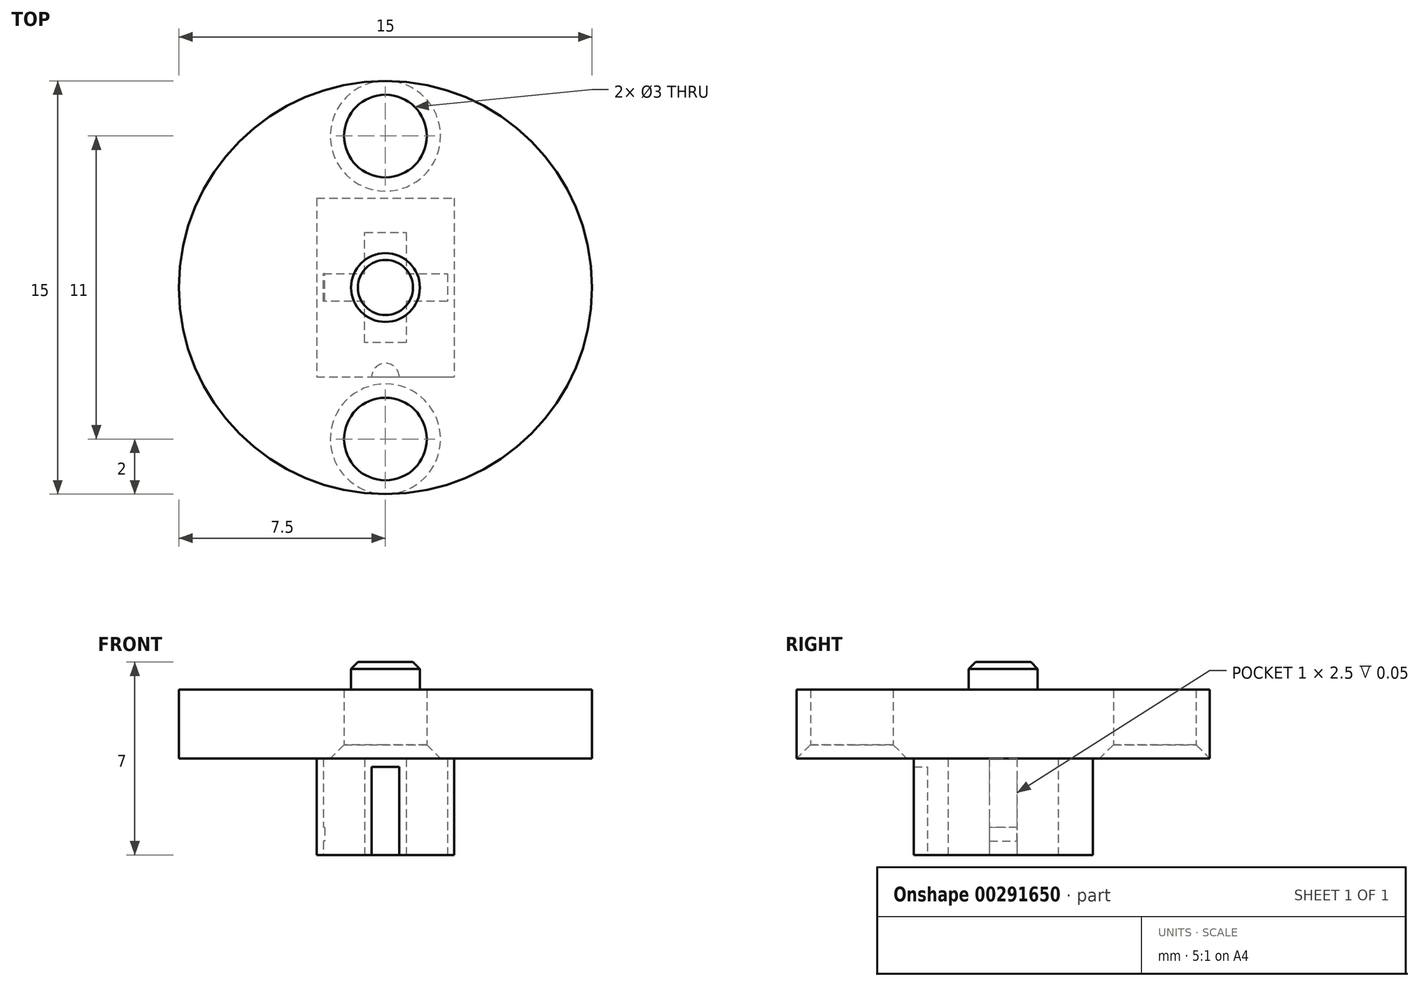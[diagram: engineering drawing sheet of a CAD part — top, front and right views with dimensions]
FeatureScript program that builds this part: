
annotation { "Feature Type Name" : "Feature", "Feature Type Description" : "" }
export const myFeature = defineFeature(function(context is Context, id is Id, definition is map)
    precondition{}
    {
        {
            var Q0;
            Q0=qCreatedBy(makeId("Top.planeOp"),FACE);
            var sketch = newSketch(context, id + "F0", { "sketchPlane" : qUnion([Q0])});
            skLineSegment(sketch, "E0", {"start": v(-0.75, -0.5) * mm, "end": v(-2.25, -0.5) * mm});
            skLineSegment(sketch, "E1", {"start": v(-2.25, -0.5) * mm, "end": v(-2.25, 0.5) * mm});
            skLineSegment(sketch, "E2", {"start": v(-2.25, 0.5) * mm, "end": v(-0.75, 0.5) * mm});
            skLineSegment(sketch, "E3", {"start": v(-0.75, 0.5) * mm, "end": v(-0.75, 2) * mm});
            skLineSegment(sketch, "E4", {"start": v(-0.75, 2) * mm, "end": v(0.75, 2) * mm});
            skLineSegment(sketch, "E5", {"start": v(0.75, 2) * mm, "end": v(0.75, 0.5) * mm});
            skLineSegment(sketch, "E6", {"start": v(0.75, 0.5) * mm, "end": v(2.25, 0.5) * mm});
            skLineSegment(sketch, "E7", {"start": v(2.25, 0.5) * mm, "end": v(2.25, -0.5) * mm});
            skLineSegment(sketch, "E8", {"start": v(2.25, -0.5) * mm, "end": v(0.75, -0.5) * mm});
            skLineSegment(sketch, "E9", {"start": v(0.75, -0.5) * mm, "end": v(0.75, -2) * mm});
            skLineSegment(sketch, "E10", {"start": v(0.75, -2) * mm, "end": v(-0.75, -2) * mm});
            skLineSegment(sketch, "E11", {"start": v(-0.75, -2) * mm, "end": v(-0.75, -0.5) * mm});
            skLineSegment(sketch, "E12.bottom", {"start": v(-2.5, 3.25) * mm, "end": v(2.5, 3.25) * mm});
            skLineSegment(sketch, "E12.top", {"start": v(-2.5, -3.25) * mm, "end": v(2.5, -3.25) * mm});
            skLineSegment(sketch, "E12.left", {"start": v(-2.5, 3.25) * mm, "end": v(-2.5, -3.25) * mm});
            skLineSegment(sketch, "E12.right", {"start": v(2.5, 3.25) * mm, "end": v(2.5, -3.25) * mm});
            skSolve(sketch);
        }
        {
            var Q0;
            Q0=makeQuery(id+"F0.imprint","IMPRINT",FACE,{"disambiguationData":[TD([[makeQuery(id+"F0.imprint","IMPRINT",EDGE,{"derivedFrom":sQuery(id+"F0.wireOp",EDGE,"E0")}),1.0]])]});
            extrude(context, id + "F1", {"entities" : qUnion([Q0]), "depth" : 3.5 * mm});
        }
        {
            var Q0;
            Q0=makeQuery(id+"F1.opExtrude","CAP_FACE",FACE,{"disambiguationData":[OSD([sQuery(id+"F0.wireOp",EDGE,"E0"),sQuery(id+"F0.wireOp",EDGE,"E1"),sQuery(id+"F0.wireOp",EDGE,"E2"),sQuery(id+"F0.wireOp",EDGE,"E3"),sQuery(id+"F0.wireOp",EDGE,"E4"),sQuery(id+"F0.wireOp",EDGE,"E5"),sQuery(id+"F0.wireOp",EDGE,"E6"),sQuery(id+"F0.wireOp",EDGE,"E7"),sQuery(id+"F0.wireOp",EDGE,"E8"),sQuery(id+"F0.wireOp",EDGE,"E9"),sQuery(id+"F0.wireOp",EDGE,"E10"),sQuery(id+"F0.wireOp",EDGE,"E11"),sQuery(id+"F0.wireOp",EDGE,"xdch3Cf1-flaN-mxDd-AqKS-SK6m0hY20tAS")])],"isStart":false});
            var sketch = newSketch(context, id + "F2", { "sketchPlane" : qUnion([Q0])});
            skCircle(sketch, "E13", {"center": v(0, 0) * mm, "radius": 7.5 * mm});
            skCircle(sketch, "E14", {"center": v(0, 5.5) * mm, "radius": 1.5 * mm});
            skCircle(sketch, "E15", {"center": v(0, -5.5) * mm, "radius": 1.5 * mm});
            skSolve(sketch);
        }
        {
            var Q0;
            Q0=makeQuery(id+"F2.imprint","IMPRINT",FACE,{"disambiguationData":[TD([[makeQuery(id+"F2.imprint","IMPRINT",EDGE,{"derivedFrom":makeQuery(id+"F1.opExtrude","CAP_EDGE",EDGE,{"disambiguationData":[OSD([sQuery(id+"F0.wireOp",EDGE,"E0")])],"isStart":false})}),-1.0]])]});
            var Q1;
            Q1=makeQuery(id+"F2.imprint","IMPRINT",FACE,{"disambiguationData":[TD([[makeQuery(id+"F2.imprint","IMPRINT",EDGE,{"derivedFrom":makeQuery(id+"F1.opExtrude","CAP_EDGE",EDGE,{"disambiguationData":[OSD([sQuery(id+"F0.wireOp",EDGE,"E0")])],"isStart":false})}),1.0]])]});
            var Q2;
            Q2=makeQuery(id+"F2.imprint","IMPRINT",FACE,{"disambiguationData":[TD([[makeQuery(id+"F2.imprint","IMPRINT",EDGE,{"derivedFrom":sQuery(id+"F2.wireOp",EDGE,"E13")}),1.0]])]});
            var Q3;
            Q3=sQuery(id+"F2.wireOp",EDGE,"E13");
            var Q4;
            Q4=sQuery(id+"F2.wireOp",EDGE,"E14");
            var Q5;
            Q5=sQuery(id+"F2.wireOp",EDGE,"E15");
            extrude(context, id + "F3", {"entities" : qUnion([Q0, Q1, Q2]), "operationType" : NewBodyOperationType.ADD, "surfaceEntities" : qUnion([Q3, Q4, Q5]), "depth" : 2.5 * mm});
        }
        {
            var Q0;
            Q0=makeQuery(id+"F3.opExtrude","CAP_FACE",FACE,{"disambiguationData":[OSD([sQuery(id+"F2.wireOp",EDGE,"E13"),sQuery(id+"F2.wireOp",EDGE,"E14"),sQuery(id+"F2.wireOp",EDGE,"E15")])],"isStart":false});
            var sketch = newSketch(context, id + "F4", { "sketchPlane" : qUnion([Q0])});
            skCircle(sketch, "E16", {"center": v(0, 0) * mm, "radius": 1.25 * mm});
            skSolve(sketch);
        }
        {
            var Q0;
            Q0=makeQuery(id+"F4.imprint","IMPRINT",FACE,{"disambiguationData":[TD([[makeQuery(id+"F4.imprint","IMPRINT",EDGE,{"derivedFrom":sQuery(id+"F4.wireOp",EDGE,"E16")}),1.0]])]});
            extrude(context, id + "F5", {"entities" : qUnion([Q0]), "operationType" : NewBodyOperationType.ADD, "depth" : 1 * mm});
        }
        {
            var Q0;
            Q0=makeQuery(id+"F3.opExtrude","CAP_EDGE",EDGE,{"disambiguationData":[OSD([sQuery(id+"F2.wireOp",EDGE,"E14")])],"isStart":true});
            var Q1;
            Q1=makeQuery(id+"F3.opExtrude","CAP_EDGE",EDGE,{"disambiguationData":[OSD([sQuery(id+"F2.wireOp",EDGE,"E15")])],"isStart":true});
            chamfer(context, id + "F6", {"entities" : qUnion([Q0, Q1]), "width" : 0.5 * mm, "tangentPropagation" : true});
        }
        {
            var Q0;
            Q0=makeQuery(id+"F5.opExtrude","CAP_EDGE",EDGE,{"disambiguationData":[OSD([sQuery(id+"F4.wireOp",EDGE,"E16")])],"isStart":false});
            chamfer(context, id + "F7", {"entities" : qUnion([Q0]), "width" : 0.25 * mm, "tangentPropagation" : true});
        }
        {
            var Q0;
            Q0=makeQuery(id+"F1.opExtrude","SWEPT_FACE",FACE,{"disambiguationData":[OSD([sQuery(id+"F0.wireOp",EDGE,"E12.left")])]});
            var sketch = newSketch(context, id + "F8", { "sketchPlane" : qUnion([Q0])});
            skLineSegment(sketch, "E17", {"start": v(0.5, 0) * mm, "end": v(0.5, 0.5) * mm});
            skLineSegment(sketch, "E18", {"start": v(0.5, 0.5) * mm, "end": v(-0.5, 0.5) * mm});
            skLineSegment(sketch, "E19", {"start": v(-0.5, 0.5) * mm, "end": v(-0.5, 1) * mm});
            skLineSegment(sketch, "E20", {"start": v(-0.5, 1) * mm, "end": v(0.5, 1) * mm});
            skLineSegment(sketch, "E21", {"start": v(0.5, 1) * mm, "end": v(0.5, 0.5) * mm});
            skSolve(sketch);
        }
        {
            var Q0;
            Q0 = qSketchRegion(id + "F8", true);
            var Q1;
            Q1=makeQuery(id+"F8.imprint","IMPRINT",FACE,{"disambiguationData":[TD([[makeQuery(id+"F8.imprint","IMPRINT",EDGE,{"derivedFrom":sQuery(id+"F8.wireOp",EDGE,"E18")}),-1.0]])]});
            extrude(context, id + "F9", {"entities" : qUnion([Q0, Q1]), "operationType" : NewBodyOperationType.ADD, "oppositeDirection" : true, "depth" : 0.3 * mm});
        }
        {
            var Q0;
            Q0=makeQuery(id+"F0.imprint","IMPRINT",FACE,{"disambiguationData":[TD([[makeQuery(id+"F0.imprint","IMPRINT",EDGE,{"derivedFrom":sQuery(id+"F0.wireOp",EDGE,"E0")}),1.0]])]});
            var sketch = newSketch(context, id + "F10", { "sketchPlane" : qUnion([Q0])});
            skCircle(sketch, "E22", {"center": v(0, -3.25) * mm, "radius": 0.5 * mm});
            skSolve(sketch);
        }
        {
            var Q0;
            Q0 = qSketchRegion(id + "F10", true);
            extrude(context, id + "F11", {"entities" : qUnion([Q0]), "operationType" : NewBodyOperationType.REMOVE, "depth" : 3.19 * mm});
        }
    });
